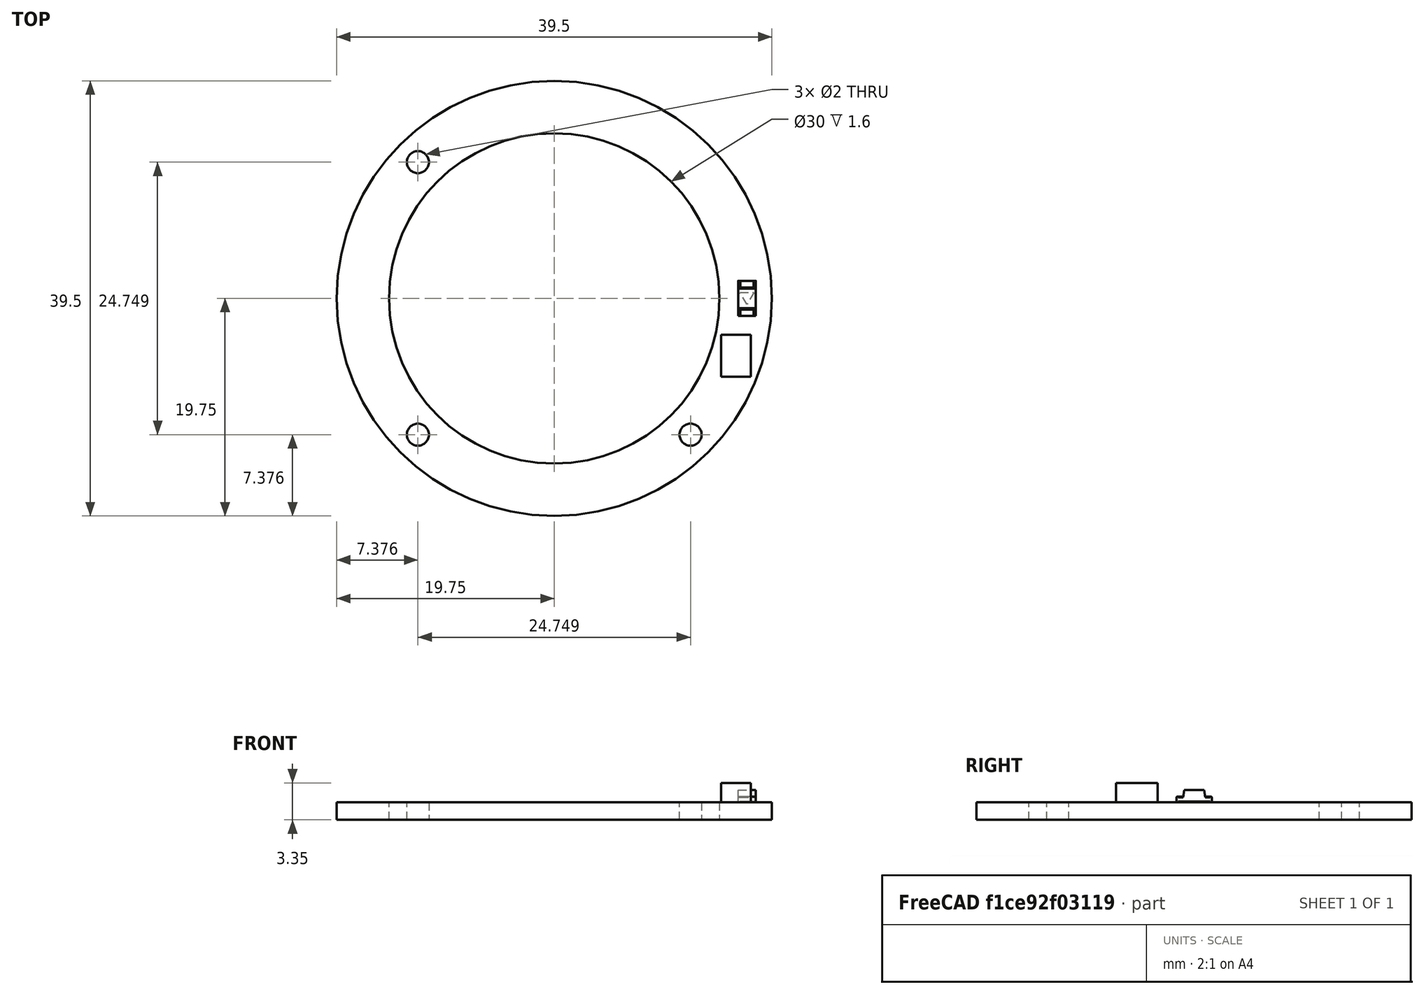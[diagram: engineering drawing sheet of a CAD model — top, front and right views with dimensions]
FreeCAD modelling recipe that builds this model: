
FCSTD DOCUMENT  (FreeCAD 1.0R39109 (Git))
Label: led_ring_pcb
License: All rights reserved
LicenseURL: https://en.wikipedia.org/wiki/All_rights_reserved
objects: App::Part×4, Part::Feature×3, App::Link×3, PartDesign::CoordinateSystem×1, Sketcher::SketchObject×1
note: 6 computed .brp shape members not serialized (recipe doc carries the construction recipe); baked Part::Feature solids carry a one-line shape summary decoded from their .brp

FEATURE [PartDesign::CoordinateSystem] Local_CS_dde3
  AttacherType = Attacher::AttachEngine3D
  MapMode = 2
FEATURE [Part::Feature] Pcb_dde3
  shape: bbox 39.5 x 39.5 x 1.6 mm, 7 faces (baked)
FEATURE [Sketcher::SketchObject] PCB_Sketch_dde3
  ArcFitTolerance = 1e-06
  FullyConstrained = true
  MakeInternals = false
  sketch-geometry (27):
    g0: Circle [constr] CenterX=137.7 CenterY=-95.2 CenterZ=0 NormalX=0 NormalY=0 NormalZ=1 AngleXU=0 Radius=19.75
    g1: Circle [constr] CenterX=137.7 CenterY=-95.2 CenterZ=0 NormalX=0 NormalY=0 NormalZ=1 AngleXU=0 Radius=15
    g2: LineSegment [constr] StartX=117.95 StartY=-114.95 StartZ=0 EndX=157.45 EndY=-114.95 EndZ=0
    g3: LineSegment [constr] StartX=157.45 StartY=-114.95 StartZ=0 EndX=157.45 EndY=-75.45 EndZ=0
    g4: LineSegment [constr] StartX=157.45 StartY=-75.45 StartZ=0 EndX=117.95 EndY=-75.45 EndZ=0
    g5: LineSegment [constr] StartX=117.95 StartY=-75.45 StartZ=0 EndX=117.95 EndY=-114.95 EndZ=0
    g6: GeomPoint [constr] X=137.7 Y=-95.2 Z=0
    g7: LineSegment StartX=117.95 StartY=-92.7 StartZ=0 EndX=117.95 EndY=-97.7 EndZ=0
    g8: LineSegment StartX=157.45 StartY=-93.7 StartZ=0 EndX=157.45 EndY=-97.7 EndZ=0
    g9: LineSegment StartX=139.2 StartY=-75.45 StartZ=0 EndX=135.2 EndY=-75.45 EndZ=0
    g10: LineSegment StartX=135.2 StartY=-114.95 StartZ=0 EndX=140.2 EndY=-114.95 EndZ=0
    g11: LineSegment [constr] StartX=117.95 StartY=-95.2 StartZ=0 EndX=157.45 EndY=-95.2 EndZ=0
    g12: LineSegment [constr] StartX=137.7 StartY=-75.45 StartZ=0 EndX=137.7 EndY=-114.95 EndZ=0
    g13: ArcOfCircle CenterX=138.25 CenterY=-95.7501 CenterZ=0 NormalX=0 NormalY=0 NormalZ=1 AngleXU=0 Radius=20.528 StartAngle=1.71993 EndAngle=2.99246
    g14: ArcOfCircle CenterX=138.25 CenterY=-94.6499 CenterZ=0 NormalX=0 NormalY=0 NormalZ=1 AngleXU=0 Radius=20.528 StartAngle=3.29073 EndAngle=4.56325
    g15: ArcOfCircle CenterX=137.15 CenterY=-94.6499 CenterZ=0 NormalX=0 NormalY=0 NormalZ=1 AngleXU=0 Radius=20.528 StartAngle=4.86152 EndAngle=6.13405
    g16: ArcOfCircle CenterX=137.7 CenterY=-95.2 CenterZ=0 NormalX=0 NormalY=0 NormalZ=1 AngleXU=0 Radius=15 StartAngle=1.47691 EndAngle=6.37707
    g17: LineSegment StartX=140.2 StartY=-79.2705 StartZ=0 EndX=140.2 EndY=-76.45 EndZ=0
    g18: LineSegment StartX=156.45 StartY=-92.7 StartZ=0 EndX=153.63 EndY=-92.7 EndZ=0
    g19: ArcOfCircle CenterX=139.2 CenterY=-79.2705 CenterZ=0 NormalX=0 NormalY=0 NormalZ=1 AngleXU=0 Radius=1 StartAngle=4.6185 EndAngle=6.28319
    g20: ArcOfCircle CenterX=139.2 CenterY=-76.45 CenterZ=0 NormalX=0 NormalY=0 NormalZ=1 AngleXU=0 Radius=1 StartAngle=4.3e-15 EndAngle=1.5708
    g21: GeomPoint [constr] X=140.2 Y=-75.45 Z=0
    g22: ArcOfCircle CenterX=153.63 CenterY=-93.7 CenterZ=0 NormalX=0 NormalY=0 NormalZ=1 AngleXU=0 Radius=1 StartAngle=1.5708 EndAngle=3.23548
    g23: ArcOfCircle CenterX=156.45 CenterY=-93.7 CenterZ=0 NormalX=0 NormalY=0 NormalZ=1 AngleXU=0 Radius=1 StartAngle=1.38e-14 EndAngle=1.5708
    g24: GeomPoint [constr] X=157.45 Y=-92.7 Z=0
    g25: LineSegment [constr] StartX=140.2 StartY=-76.45 StartZ=0 EndX=137.7 EndY=-76.45 EndZ=0
    g26: LineSegment [constr] StartX=156.45 StartY=-92.7 StartZ=0 EndX=156.45 EndY=-95.2 EndZ=0
  constraints (71):
    c: Coincident(g2,g3)
    c: Coincident(g3,g4)
    c: Coincident(g4,g5)
    c: Coincident(g5,g2)
    c: Horizontal(g2)
    c: Horizontal(g4)
    c: Vertical(g3)
    c: Vertical(g5)
    c: Symmetric(g4,g2,g6)
    c: Coincident(g6,g0)
    c: Diameter(g0) = 39.5
    c: Coincident(g0,g1)
    c: DistanceX(g0) = 137.7
    c: DistanceY(g0) = -95.2
    c: Tangent(g4,g0)
    c: Tangent(g3,g0)
    c: PointOnObject(g7,g5)
    c: PointOnObject(g7,g5)
    c: PointOnObject(g24,g3)
    c: PointOnObject(g21,g4)
    c: PointOnObject(g9,g4)
    c: PointOnObject(g10,g2)
    c: DistanceX(g9,g21) = 5
    c: PointOnObject(g11,g0)
    c: Symmetric(g3,g3,g11)
    c: PointOnObject(g12,g9)
    c: Symmetric(g2,g2,g12)
    c: Symmetric(g21,g9,g12)
    c: Symmetric(g7,g7,g11)
    c: Symmetric(g24,g8,g11)
    c: Symmetric(g10,g10,g12)
    c: Diameter(g1) = 30
    c: Coincident(g13,g9)
    c: Coincident(g13,g7)
    c: Tangent(g13,g0)
    c: Coincident(g14,g7)
    c: Coincident(g14,g10)
    c: Tangent(g14,g0)
    c: Coincident(g15,g10)
    c: Coincident(g15,g8)
    c: Tangent(g15,g0)
    c: Equal(g16,g1)
    c: Tangent(g17,g19) = -1.5708
    c: Tangent(g16,g19) = 1.5708
    c: PointOnObject(g21,g17)
    c: PointOnObject(g21,g9)
    c: Tangent(g17,g20) = -1.5708
    c: Tangent(g9,g20) = -1.5708
    c: Tangent(g18,g22) = -1.5708
    c: Tangent(g16,g22) = 1.5708
    c: PointOnObject(g24,g18)
    c: PointOnObject(g24,g8)
    c: Tangent(g18,g23) = -1.5708
    c: Tangent(g8,g23) = 1.5708
    c: Equal(g20,g19)
    c: Equal(g19,g23)
    c: Equal(g23,g22)
    c: PointOnObject(g16,g1)
    c: Vertical(g17)
    c: Horizontal(g18)
    c: Radius(g19) = 1
    c: PointOnObject(g16,g12)
    c: Coincident(g25,g17)
    c: PointOnObject(g25,g12)
    c: Horizontal(g25)
    c: Coincident(g26,g18)
    c: PointOnObject(g26,g11)
    c: Vertical(g26)
    c: Equal(g26,g25)
    c: Vertical(g9,g10)
    c: Horizontal(g7,g8)
FEATURE [App::Part] Board_Geoms_dde3
  Group = -> [Pcb_dde3,PCB_Sketch_dde3]
  Origin = -> Origin
FEATURE [Part::Feature] Shape  label="D4_LED_1206_3216Metric_4427d1468fe1"
  Placement = pos=(155.2,-95.2,0) rot=(0,0,1;1.5708rad)
  shape: bbox 1.6 x 3.2 x 1.1 mm, 50 faces (baked)
FEATURE [Part::Feature] Shape001  label="J1_Body_c86f84fccd7c[2]"
  Placement = pos=(154.2,-100.4,0) rot=(0,0,1;1.5708rad)
  shape: bbox 2.7 x 3.8 x 1.75 mm, 6 faces (baked)
FEATURE [App::Link] D4_LED_1206_3216Metric_4427d1468fe1_ln_  label="D3_LED_1206_3216Metric_26d53b740720"
  LinkPlacement = pos=(137.7,-112.7,0) rot=(0,0,1;3.14159rad)
  LinkedObject = -> Shape
  Placement = pos=(137.7,-112.7,0) rot=(0,0,1;3.14159rad)
FEATURE [App::Link] D4_LED_1206_3216Metric_4427d1468fe1_ln_001  label="D1_LED_1206_3216Metric_f67cb64cced4"
  LinkPlacement = pos=(137.7,-77.7,0) rot=(0,0,1;0rad)
  LinkedObject = -> Shape
  Placement = pos=(137.7,-77.7,0) rot=(0,0,1;0rad)
FEATURE [App::Link] D4_LED_1206_3216Metric_4427d1468fe1_ln_002  label="D2_LED_1206_3216Metric_5a2045abea7a"
  LinkPlacement = pos=(120.2,-95.2,0) rot=(0,0,1;1.5708rad)
  LinkedObject = -> Shape
  Placement = pos=(120.2,-95.2,0) rot=(0,0,1;1.5708rad)
FEATURE [App::Part] Top_dde3
  Group = -> [Shape,Shape001,D4_LED_1206_3216Metric_4427d1468fe1_ln_,D4_LED_1206_3216Metric_4427d1468fe1_ln_001,D4_LED_1206_3216Metric_4427d1468fe1_ln_002]
  Origin = -> Origin003
FEATURE [App::Part] Step_Models_dde3
  Group = -> [Top_dde3]
  Origin = -> Origin002
FEATURE [App::Part] Board_dde3  label="led_ring_pcb"
  Group = -> [Local_CS_dde3,Board_Geoms_dde3,Step_Models_dde3]
  Origin = -> Origin001
